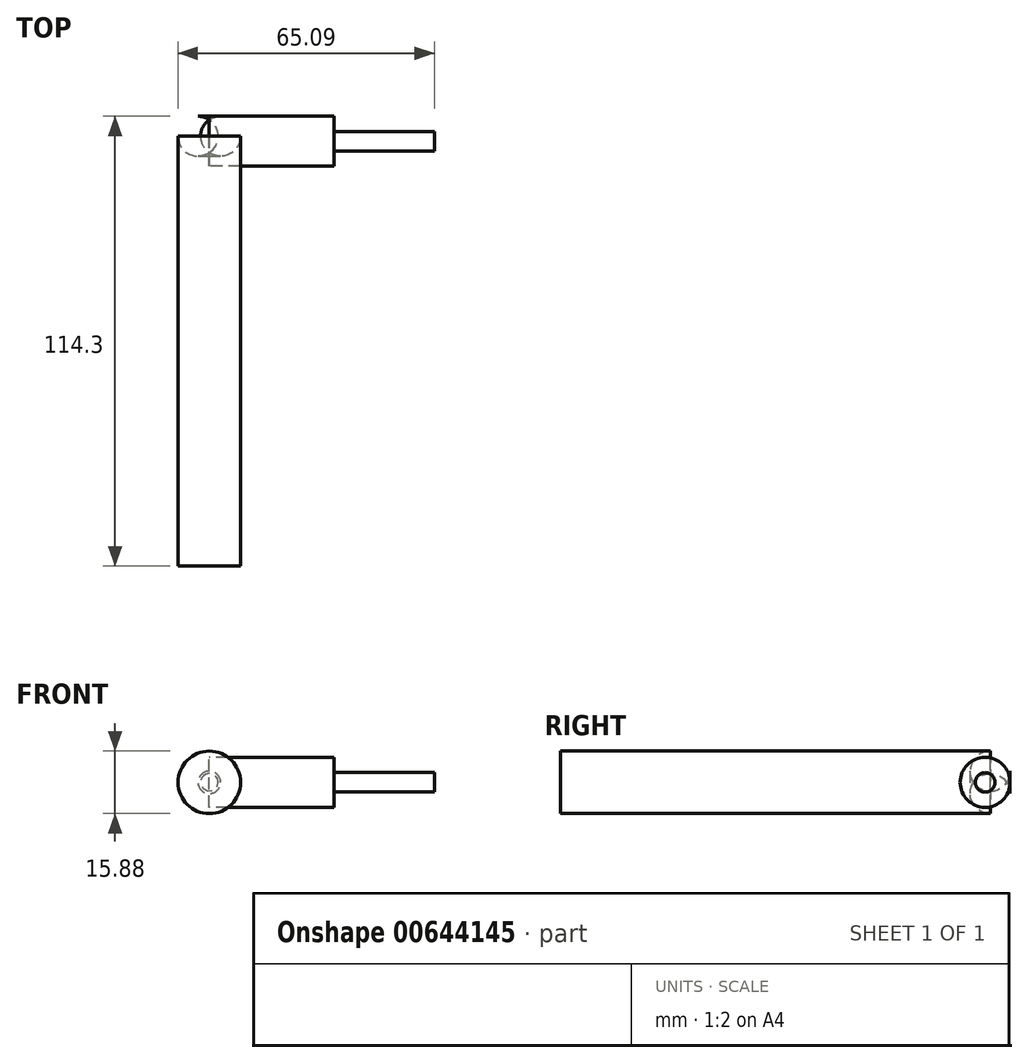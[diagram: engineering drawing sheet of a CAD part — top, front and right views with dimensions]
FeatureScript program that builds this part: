
annotation { "Feature Type Name" : "Feature", "Feature Type Description" : "" }
export const myFeature = defineFeature(function(context is Context, id is Id, definition is map)
    precondition{}
    {
        {
            var Q0;
            Q0=qCreatedBy(makeId("Front.planeOp"),FACE);
            var sketch = newSketch(context, id + "F0", { "sketchPlane" : qUnion([Q0])});
            skCircle(sketch, "E0", {"center": v(0, 0) * mm, "radius": 7.94 * mm});
            skSolve(sketch);
        }
        {
            var Q0;
            Q0=makeQuery(id+"F0.imprint","IMPRINT",FACE,{"disambiguationData":[TD([[makeQuery(id+"F0.imprint","IMPRINT",EDGE,{"derivedFrom":sQuery(id+"F0.wireOp",EDGE,"E0")}),1.0]])]});
            extrude(context, id + "F1", {"entities" : qUnion([Q0]), "depth" : 114.3 * mm, "offsetDistance" : 25.4 * mm});
        }
        {
            var Q0;
            Q0=qCreatedBy(makeId("Right.planeOp"),FACE);
            var sketch = newSketch(context, id + "F2", { "sketchPlane" : qUnion([Q0])});
            skCircle(sketch, "E1", {"center": v(-6.35, 0) * mm, "radius": 6.35 * mm});
            skSolve(sketch);
        }
        {
            var Q0;
            Q0 = qSketchRegion(id + "F2", true);
            var Q1;
            Q1=sQuery(id+"F2.wireOp",EDGE,"E1");
            extrude(context, id + "F3", {"entities" : qUnion([Q0]), "surfaceEntities" : qUnion([Q1]), "depth" : 31.75 * mm, "offsetDistance" : 25.4 * mm});
        }
        {
            var Q0;
            Q0=makeQuery(id+"F1.opExtrude","CAP_EDGE",EDGE,{"disambiguationData":[OSD([sQuery(id+"F0.wireOp",EDGE,"E0")])],"isStart":true});
            fillet(context, id + "F4", {"entities" : qUnion([Q0]), "radius" : 5.08 * mm, "tangentPropagation" : true, "allowEdgeOverflow" : false});
        }
        {
            var Q0;
            Q0=makeQuery(id+"F3.opExtrude","CAP_FACE",FACE,{"disambiguationData":[OSD([sQuery(id+"F2.wireOp",EDGE,"E1")])],"isStart":false});
            var sketch = newSketch(context, id + "F5", { "sketchPlane" : qUnion([Q0])});
            skCircle(sketch, "E2", {"center": v(-6.35, 0) * mm, "radius": 2.48 * mm});
            skSolve(sketch);
        }
        {
            var Q0;
            Q0=makeQuery(id+"F5.imprint","IMPRINT",FACE,{"disambiguationData":[TD([[makeQuery(id+"F5.imprint","IMPRINT",EDGE,{"derivedFrom":sQuery(id+"F5.wireOp",EDGE,"E2")}),1.0]])]});
            extrude(context, id + "F6", {"entities" : qUnion([Q0]), "operationType" : NewBodyOperationType.ADD, "depth" : 25.4 * mm, "offsetDistance" : 25.4 * mm});
        }
    });
